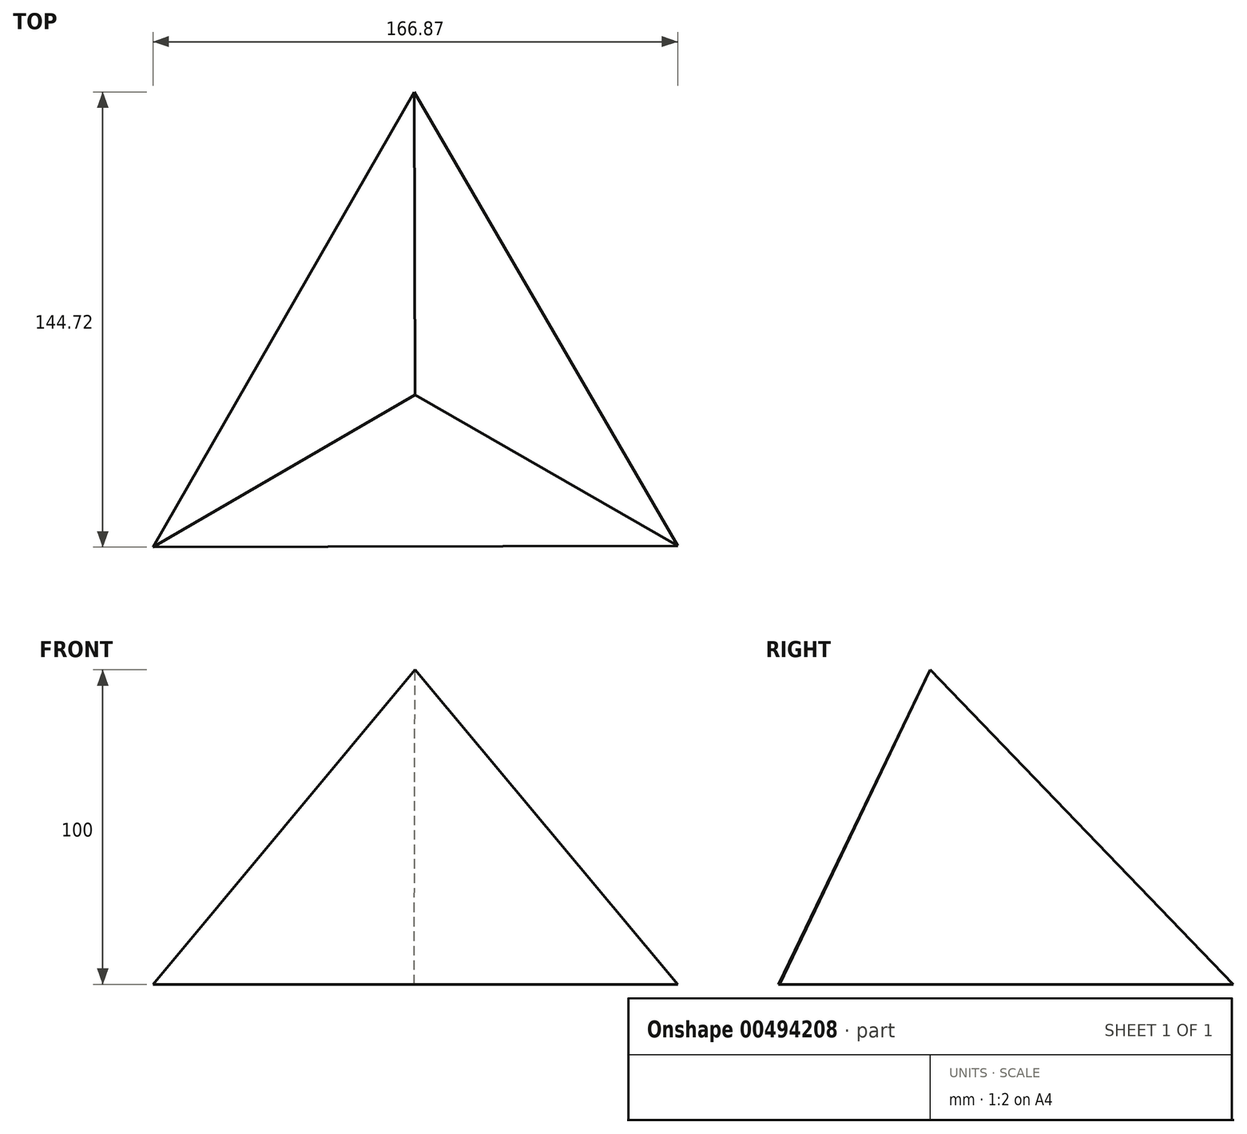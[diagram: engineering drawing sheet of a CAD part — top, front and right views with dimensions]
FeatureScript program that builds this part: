
annotation { "Feature Type Name" : "Feature", "Feature Type Description" : "" }
export const myFeature = defineFeature(function(context is Context, id is Id, definition is map)
    precondition{}
    {
        {
            var Q0;
            Q0=qCreatedBy(makeId("Top.planeOp"),FACE);
            var sketch = newSketch(context, id + "F0", { "sketchPlane" : qUnion([Q0])});
            skCircle(sketch, "E0.cCircle", {"center": v(0, 0) * mm, "radius": 96.35 * mm, "construction": true});
            skLineSegment(sketch, "E0.0", {"start": v(83.55, -47.98) * mm, "end": v(-83.32, -48.37) * mm});
            skLineSegment(sketch, "E0.1", {"start": v(-83.32, -48.37) * mm, "end": v(-0.23, 96.35) * mm});
            skLineSegment(sketch, "E0.2", {"start": v(-0.23, 96.35) * mm, "end": v(83.55, -47.98) * mm});
            skSolve(sketch);
        }
        {
            var Q0;
            Q0=qCreatedBy(makeId("Top.planeOp"),FACE);
            cPlane(context, id + "F1", {"entities" : qUnion([Q0]), "cplaneType" : CPlaneType.OFFSET, "offset" : 100 * mm, "width" : 150 * mm, "height" : 150 * mm});
        }
        {
            var Q0;
            Q0=qCreatedBy(id+"F1.planeOp",FACE);
            var sketch = newSketch(context, id + "F2", { "sketchPlane" : qUnion([Q0])});
            skPoint(sketch, "E1", {"position": v(0, 0) * mm});
            skSolve(sketch);
        }
        {
            var Q0;
            Q0=makeQuery(id+"F0.imprint","IMPRINT",FACE,{"disambiguationData":[TD([[makeQuery(id+"F0.imprint","IMPRINT",EDGE,{"derivedFrom":sQuery(id+"F0.wireOp",EDGE,"E0.0")}),-1.0]])]});
            var Q1;
            Q1=sQuery(id+"F2.wireOp",VERTEX,"E1");
            loft(context, id + "F3", {"sheetProfilesArray" : [{ "sheetProfileEntities" : qUnion([Q0]) }, { "sheetProfileEntities" : qUnion([Q1]) }]});
        }
    });
